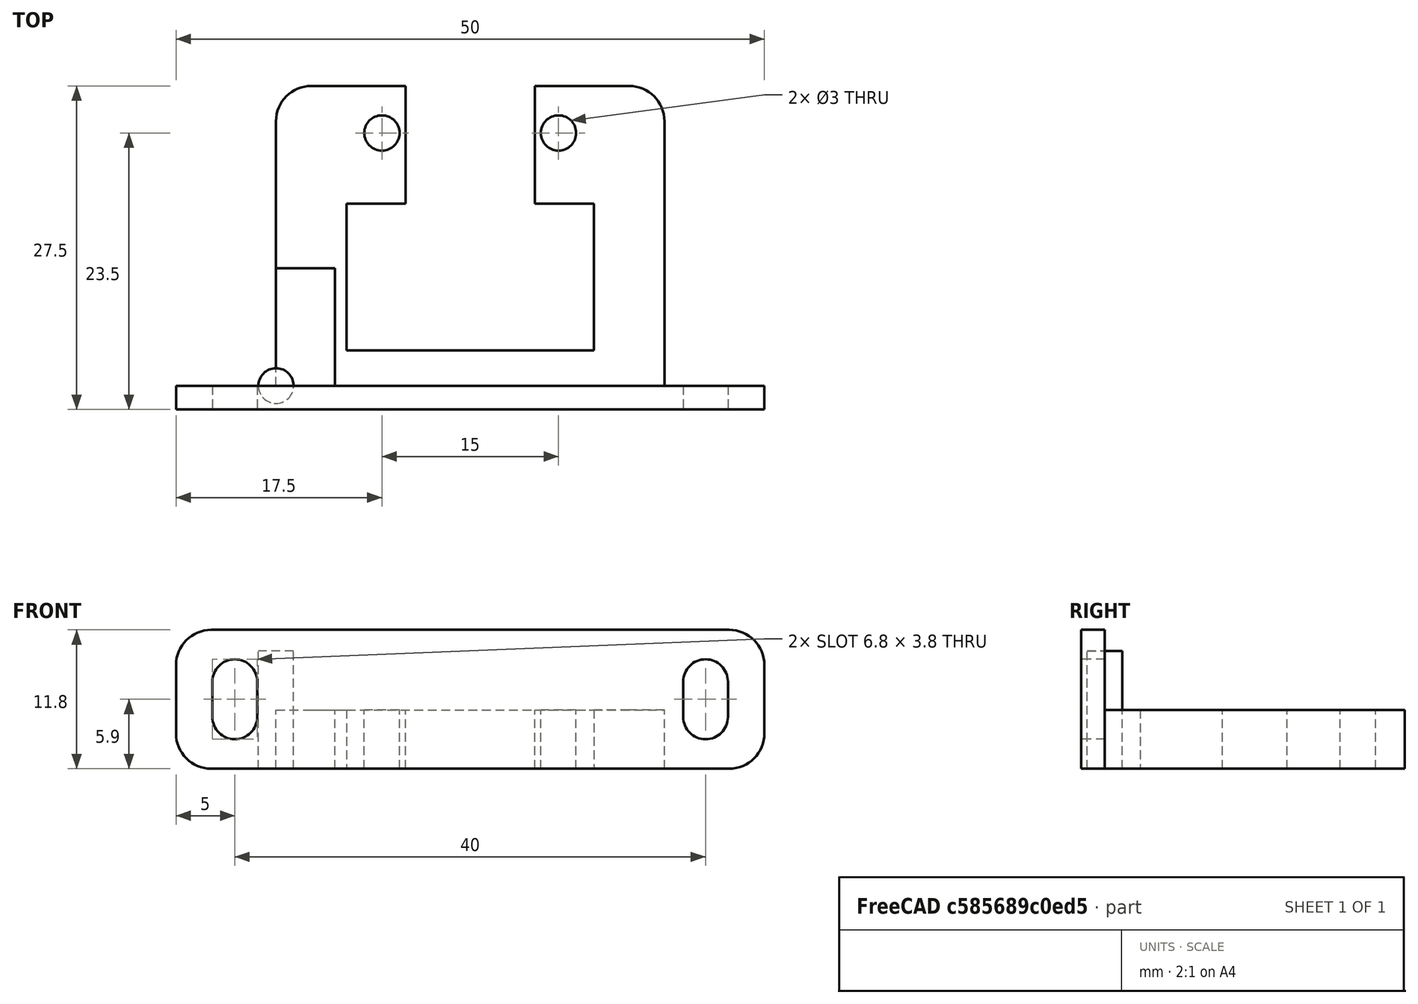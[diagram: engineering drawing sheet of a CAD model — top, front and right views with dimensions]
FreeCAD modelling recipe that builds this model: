
FCSTD DOCUMENT  (FreeCAD 0.19R23578 (Git))
Label: gy-219_ina219
License: All rights reserved
LicenseURL: http://en.wikipedia.org/wiki/All_rights_reserved
objects: Part::Box×3, Part::FeaturePython×2, Spreadsheet::Sheet×1, Part::Cylinder×1, Part::Fillet×1, Part::Mirroring×1, Part::Feature×1, Part::MultiFuse×1, Part::Cut×1, App::Part×1
note: 9 computed .brp shape members not serialized (recipe doc carries the construction recipe); baked Part::Feature solids carry a one-line shape summary decoded from their .brp

FEATURE [Part::Box] Box  label="side stand cube"
  AttacherType = Attacher::AttachEngine3D
  Height = 5
  Length = 6
  Width = 25.5
  expr: Height = <<p>>.stand_thickness
  expr: Width = <<p>>.pcb_y + <<p>>.under_stand_pad
  expr: Length = <<p>>.stand_x_width
FEATURE [Spreadsheet::Sheet] Spreadsheet  label="p"
  cells = A1=pcb_x; B1(pcb_x)==21mm; A2=pcb_y; B2(pcb_y)==22.5mm; A3=pcb_z; B3(pcb_z)==1.8mm; A4=hole_off_y; B4(hole_off_y)==4mm; A5=hole_dist_x; B5(hole_dist_x)==15mm; A6=hole_r; B6(hole_r)==1.5mm; A7=under_stand_pad; B7(under_stand_pad)==3mm; A8=stand_thickness; B8(stand_thickness)==5mm; A9=stand_x_width; B9(stand_x_width)==6mm; A10=hole_stand_size_x; B10(hole_stand_size_x)==5mm; A11=hole_stand_size_y; B11(hole_stand_size_y)==10mm
FEATURE [Part::Box] Box001  label="bottom pad"
  AttacherType = Attacher::AttachEngine3D
  Height = 5
  Length = 33
  Width = 3
  expr: Height = <<p>>.stand_thickness
  expr: Length = <<p>>.pcb_x + <<p>>.stand_x_width * 2
  expr: Width = <<p>>.under_stand_pad
FEATURE [Part::Box] Box002  label="pcb hole stand"
  AttacherType = Attacher::AttachEngine3D
  Height = 5
  Length = 5
  Width = 10
  expr: Length = <<p>>.hole_stand_size_x
  expr: Height = <<p>>.stand_thickness
  expr: Width = <<p>>.hole_stand_size_y
FEATURE [Part::FeaturePython] Array001  label="pcb hole stand array"  # Draft array (typed FeaturePython)
  Angle = 360
  ArrayType = 0
  Axis = (0,0,1)
  Base = -> Box002
  Center = (0,0,0)
  Count = 2
  ExpandArray = false
  Fuse = false
  IntervalAxis = (0,0,0)
  IntervalX = (16,0,0)
  IntervalY = (0,100,0)
  IntervalZ = (0,0,100)
  NumberCircles = 3
  NumberPolar = 5
  NumberX = 2
  NumberY = 1
  NumberZ = 1
  Placement = pos=(6,15.5,0) rot=(0,0,1;0rad)
  PlacementList = 2 placements: [(0,0,0),(16,0,0)]
  RadialDistance = 50
  ScaleList = (2) [(1,1,1),(1,1,1)]
  Symmetry = 1
  TangentialDistance = 25
  expr: .IntervalX.x = <<p>>.pcb_x - <<p>>.hole_stand_size_x
  expr: .Placement.Base.x = <<p>>.stand_x_width
  expr: .Placement.Base.y = <<p>>.under_stand_pad + <<p>>.pcb_y - <<p>>.hole_stand_size_y
FEATURE [Part::Cylinder] Cylinder  label="hole"
  Angle = 360
  AttacherType = Attacher::AttachEngine3D
  Height = 10
  Radius = 1.5
  expr: Radius = <<p>>.hole_r
FEATURE [Part::FeaturePython] Array002  label="hole array"  # Draft array (typed FeaturePython)
  Angle = 360
  ArrayType = 0
  Axis = (0,0,1)
  Base = -> Cylinder
  Center = (0,0,0)
  Count = 2
  ExpandArray = false
  Fuse = false
  IntervalAxis = (0,0,0)
  IntervalX = (15,0,0)
  IntervalY = (0,100,0)
  IntervalZ = (0,0,100)
  NumberCircles = 3
  NumberPolar = 5
  NumberX = 2
  NumberY = 1
  NumberZ = 1
  Placement = pos=(9,21.5,0) rot=(0,0,1;0rad)
  PlacementList = 2 placements: [(0,0,0),(15,0,0)]
  RadialDistance = 50
  ScaleList = (2) [(1,1,1),(1,1,1)]
  Symmetry = 1
  TangentialDistance = 25
  expr: .IntervalX.x = <<p>>.hole_dist_x
  expr: .Placement.Base.x = (<<p>>.pcb_x + <<p>>.stand_x_width * 2 - <<p>>.hole_dist_x) / 2
  expr: .Placement.Base.y = <<p>>.under_stand_pad + <<p>>.pcb_y - <<p>>.hole_off_y
FEATURE [Part::Fillet] Fillet  label="side stand fillet"
  Base = -> Box
  Edges = 1 edges r=3: [Edge3]
FEATURE [Part::Mirroring] Part__Mirroring  label="side stand cube (Mirror #1)"
  Base = (16.5,0,0)
  Normal = (1,0,0)
  Source = -> Fillet
  expr: .Base.x = <<p>>.pcb_x - <<p>>.stand_x_width * 3 / 4
FEATURE [Part::Feature] Body002  label="attach plane x rotated dir001"
  Placement = pos=(-8.5,0,0) rot=(1,0,0;1.5708rad)
  shape: bbox 50 x 2 x 11.8 mm, 18 faces (baked)
FEATURE [Part::MultiFuse] Fusion  label="stand fusion"
  Shapes = -> [Array001,Box001,Fillet,Part__Mirroring,Body002]
FEATURE [Part::Cut] Cut  label="body cut"
  Base = -> Fusion
  Tool = -> Array002
FEATURE [App::Part] Part  label="body part"
  Group = -> [Box002,Array001,Box001,Cylinder,Array002,Fusion,Cut]
  Origin = -> Origin
